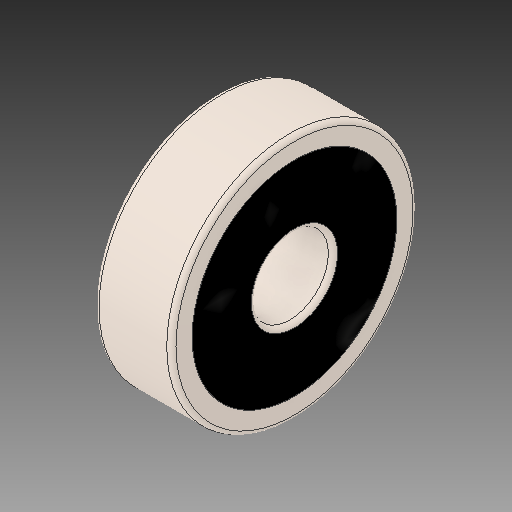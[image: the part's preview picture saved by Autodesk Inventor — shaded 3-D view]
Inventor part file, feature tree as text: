
AUTODESK INVENTOR PART (.ipt)
format: ipt  version: 2018 (Build 220112000, 112)  size: 2,300,928 bytes
history: imported  units: mm
features: other x22, sketch x2, imported_body x1
ambient origin geometry x8: Origin, YZ Plane, XZ Plane, XY Plane, X Axis, Y Axis, Z Axis, Center Point
bodies: Solid1 (imported_parasolid), Solid2 (imported_parasolid), Solid3 (imported_parasolid), Solid4 (imported_parasolid), Solid5 (imported_parasolid), Solid6 (imported_parasolid), Solid7 (imported_parasolid), Solid8 (imported_parasolid), Solid9 (imported_parasolid), Solid10 (imported_parasolid), Solid11 (imported_parasolid), Solid12 (imported_parasolid), Solid13 (imported_parasolid), Solid14 (imported_parasolid), Solid15 (imported_parasolid), Solid16 (imported_parasolid), Solid17 (imported_parasolid), Solid18 (imported_parasolid), Solid19 (imported_parasolid), Solid20 (imported_parasolid)
feature tree (25):
  other  "SKF 625_CPY.ipt"
  other  "Solid1::SKF 625_CPY.ipt"
  other  "Solid2::SKF 625_CPY.ipt"
  other  "Solid3::SKF 625_CPY.ipt"
  other  "Solid4::SKF 625_CPY.ipt"
  other  "Solid5::SKF 625_CPY.ipt"
  other  "Solid6::SKF 625_CPY.ipt"
  other  "Solid7::SKF 625_CPY.ipt"
  other  "Solid8::SKF 625_CPY.ipt"
  other  "Solid9::SKF 625_CPY.ipt"
  other  "Solid10::SKF 625_CPY.ipt"
  other  "Solid11::SKF 625_CPY.ipt"
  other  "Solid12::SKF 625_CPY.ipt"
  other  "Solid13::SKF 625_CPY.ipt"
  other  "Solid14::SKF 625_CPY.ipt"
  other  "Solid15::SKF 625_CPY.ipt"
  other  "Solid16::SKF 625_CPY.ipt"
  other  "Solid17::SKF 625_CPY.ipt"
  other  "Solid18::SKF 625_CPY.ipt"
  other  "Solid19::SKF 625_CPY.ipt"
  other  "Solid20::SKF 625_CPY.ipt"
  other  "TaggingFeature1"
  sketch  "Sketch1"  dims[d0=10.0mm]
  sketch  "Sketch2"
  imported_body  NMx_Import_Brep_tag  [imported B-rep: ~49 faces, bbox_mm=None]
